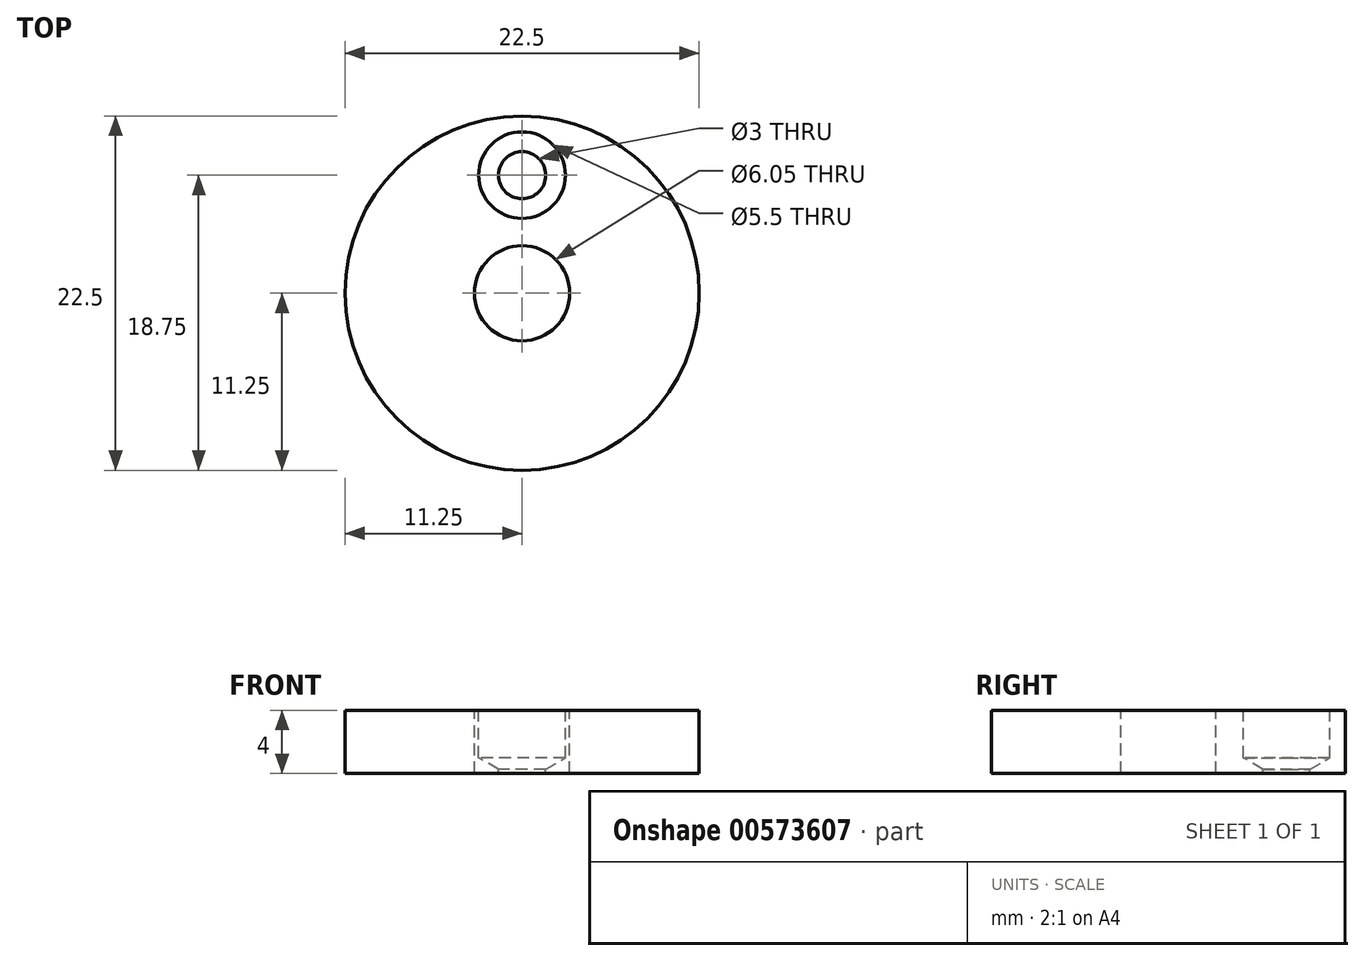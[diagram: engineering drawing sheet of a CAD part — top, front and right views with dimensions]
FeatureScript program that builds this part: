
annotation { "Feature Type Name" : "Feature", "Feature Type Description" : "" }
export const myFeature = defineFeature(function(context is Context, id is Id, definition is map)
    precondition{}
    {
        {
            var Q0;
            Q0=qCreatedBy(makeId("Top.planeOp"),FACE);
            var sketch = newSketch(context, id + "F0", { "sketchPlane" : qUnion([Q0])});
            skCircle(sketch, "E0", {"center": v(0, 0) * mm, "radius": 11.25 * mm});
            skSolve(sketch);
        }
        {
            var Q0;
            Q0 = qSketchRegion(id + "F0", true);
            extrude(context, id + "F1", {"entities" : qUnion([Q0]), "depth" : 4 * mm, "offsetDistance" : 25.4 * mm});
        }
        {
            var Q0;
            Q0=makeQuery(id+"F1.opExtrude","CAP_FACE",FACE,{"disambiguationData":[OSD([sQuery(id+"F0.wireOp",EDGE,"E0")])],"isStart":false});
            var sketch = newSketch(context, id + "F2", { "sketchPlane" : qUnion([Q0])});
            skCircle(sketch, "E1", {"center": v(0, 0) * mm, "radius": 7.5 * mm});
            skPoint(sketch, "E2", {"position": v(0, 7.5) * mm});
            skSolve(sketch);
        }
        {
            var Q0;
            Q0=sQuery(id+"F2.wireOp",VERTEX,"E2");
            var Q1;
            Q1=makeQuery(id+"F1.opExtrude","SWEPT_BODY",BODY,{"disambiguationData":[OSD([sQuery(id+"F0.wireOp",EDGE,"E0")])]});
            hole(context, id + "F3", {"style" : HoleStyle.SIMPLE, "endStyle" : HoleEndStyle.THROUGH, "holeDiameter" : 3 * mm, "isTappedThrough" : true, "tappedDepth" : 12.7 * mm, "tapClearance" : 3, "locations" : qUnion([Q0]), "scope" : qUnion([Q1]), "majorDiameter" : 5 * mm});
        }
        {
            var Q0;
            Q0=makeQuery(id+"F1.opExtrude","CAP_FACE",FACE,{"disambiguationData":[OSD([sQuery(id+"F0.wireOp",EDGE,"E0")])],"isStart":false});
            var sketch = newSketch(context, id + "F4", { "sketchPlane" : qUnion([Q0])});
            skCircle(sketch, "E3", {"center": v(0, 0) * mm, "radius": 3.02 * mm});
            skSolve(sketch);
        }
        {
            var Q0;
            Q0=sQuery(id+"F4.wireOp",VERTEX,"E3.center");
            var Q1;
            Q1=makeQuery(id+"F1.opExtrude","SWEPT_BODY",BODY,{"disambiguationData":[OSD([sQuery(id+"F0.wireOp",EDGE,"E0")])]});
            hole(context, id + "F5", {"style" : HoleStyle.SIMPLE, "endStyle" : HoleEndStyle.THROUGH, "holeDiameter" : 6.05 * mm, "isTappedThrough" : true, "tappedDepth" : 12.7 * mm, "tapClearance" : 3, "locations" : qUnion([Q0]), "scope" : qUnion([Q1])});
        }
        {
            var Q0;
            Q0=sQuery(id+"F2.wireOp",VERTEX,"E2");
            var Q1;
            Q1=makeQuery(id+"F1.opExtrude","SWEPT_BODY",BODY,{"disambiguationData":[OSD([sQuery(id+"F0.wireOp",EDGE,"E0")])]});
            hole(context, id + "F6", {"style" : HoleStyle.SIMPLE, "endStyle" : HoleEndStyle.BLIND, "holeDiameter" : 5.5 * mm, "majorDiameter" : 5 * mm, "holeDepth" : 3 * mm, "isTappedThrough" : true, "tappedDepth" : 12.7 * mm, "tapClearance" : 3, "locations" : qUnion([Q0]), "scope" : qUnion([Q1])});
        }
    });
